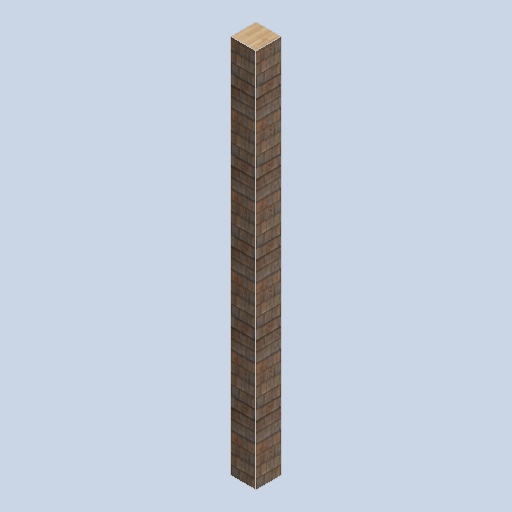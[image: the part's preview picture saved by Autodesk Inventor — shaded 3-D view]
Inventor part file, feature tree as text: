
AUTODESK INVENTOR PART (.ipt)
format: ipt  version: 2024.2 (Build 282272000, 272)  size: 135,680 bytes
history: native  units: in
note: dims shown in document units (in); Inventor stores cm internally (conversion verified against a paired STEP export)
features: other x3, sketch x1
ambient origin geometry x8: Origin, YZ Plane, XZ Plane, XY Plane, X Axis, Y Axis, Z Axis, Center Point
bodies: Solid1 (feature_tree)
feature tree (4):
  other  "support_frame_03_MIR.ipt"
  other  "Solid1::support_frame_03_MIR.ipt"
  other  "TaggingFeature1"
  sketch  "Sketch1"  dims[d0=0.3937in]
